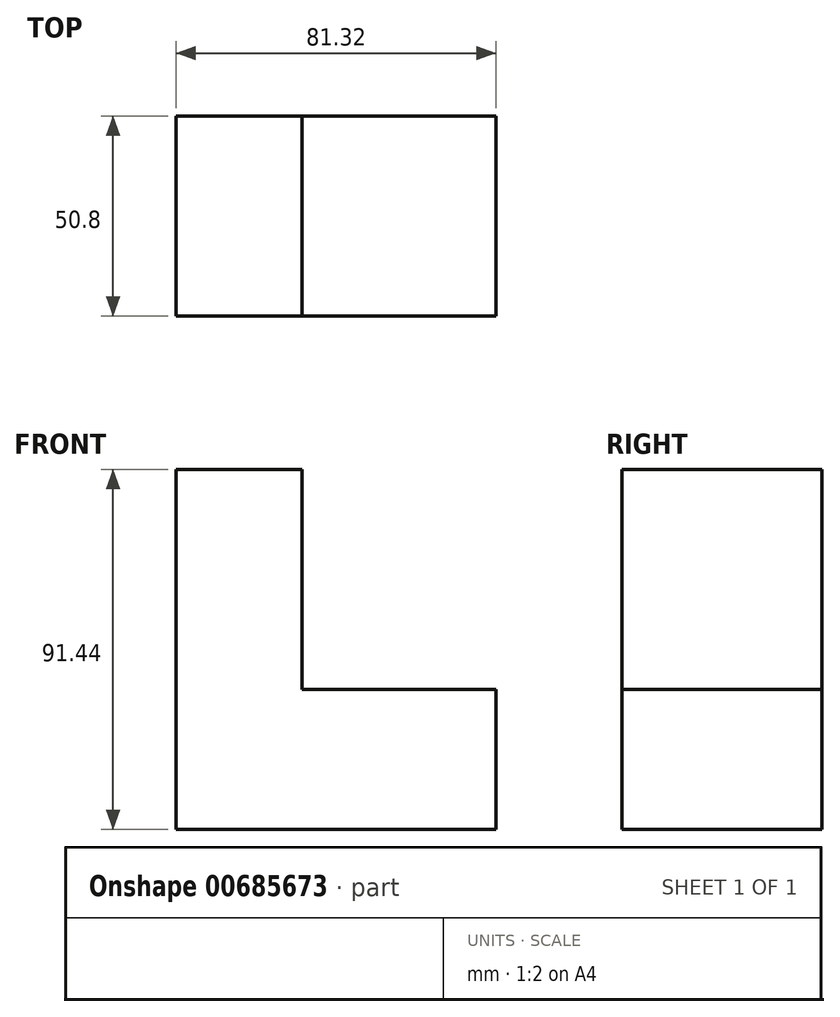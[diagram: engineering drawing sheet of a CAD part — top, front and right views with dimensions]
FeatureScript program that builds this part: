
annotation { "Feature Type Name" : "Feature", "Feature Type Description" : "" }
export const myFeature = defineFeature(function(context is Context, id is Id, definition is map)
    precondition{}
    {
        {
            var Q0;
            Q0=qCreatedBy(makeId("Front.planeOp"),FACE);
            var sketch = newSketch(context, id + "F0", { "sketchPlane" : qUnion([Q0])});
            skLineSegment(sketch, "E0", {"start": v(0, 0) * mm, "end": v(0, 55.84) * mm});
            skLineSegment(sketch, "E1", {"start": v(0, 55.84) * mm, "end": v(-31.96, 55.84) * mm});
            skLineSegment(sketch, "E2", {"start": v(-31.96, 55.84) * mm, "end": v(-31.96, 0) * mm});
            skLineSegment(sketch, "E3", {"start": v(-31.96, 0) * mm, "end": v(-31.96, -35.6) * mm});
            skLineSegment(sketch, "E4", {"start": v(-31.96, -35.6) * mm, "end": v(49.36, -35.6) * mm});
            skLineSegment(sketch, "E5", {"start": v(49.36, -35.6) * mm, "end": v(49.36, 0) * mm});
            skLineSegment(sketch, "E6", {"start": v(49.36, 0) * mm, "end": v(0, 0) * mm});
            skSolve(sketch);
        }
        {
            var Q0;
            Q0=makeQuery(id+"F0.imprint","IMPRINT",FACE,{"disambiguationData":[TD([[makeQuery(id+"F0.imprint","IMPRINT",EDGE,{"derivedFrom":sQuery(id+"F0.wireOp",EDGE,"E0")}),1.0]])]});
            extrude(context, id + "F1", {"entities" : qUnion([Q0]), "depth" : 50.8 * mm, "offsetDistance" : 25.4 * mm});
        }
    });
